# Revit family: Profim LightUP
name_source: partatom
category: Furniture
revit_build: Autodesk Revit Architecture 2015 (Build: 20140322_1515(x64)
units: mm (PartAtom-declared; Revit-internal decimal feet)

## types (1)
- Profim LightUP 250SFL
    Armrest material = ProfiM - lightUP - Armrest
    Back Frame material = ProfiM - lightUP - Back frame
    Backrest material = ProfiM - lightUP - Backrest
    Base material = ProfiM - lightUP - Base
    Damper Lower material = ProfiM - lightUP - Damper lower
    Damper Upper material = ProfiM - lightUP - Damper upper
    Description = swivel armchair, medium backrest, 5-star base on wheels
    Manufacturer = Profim
    Model = LightUP 250SFL
    Seat Frame material = ProfiM - lightUP - Seat Frame
    Seat Mechanism material = ProfiM - lightUP - Seat Mechanism
    Seat material = ProfiM - lightUP - Seat
    Wheels material = ProfiM - lightUP - Wheels

## geometry (parser evidence)
native form markers: Sweep x2
no freeform markers — native parametric forms only
